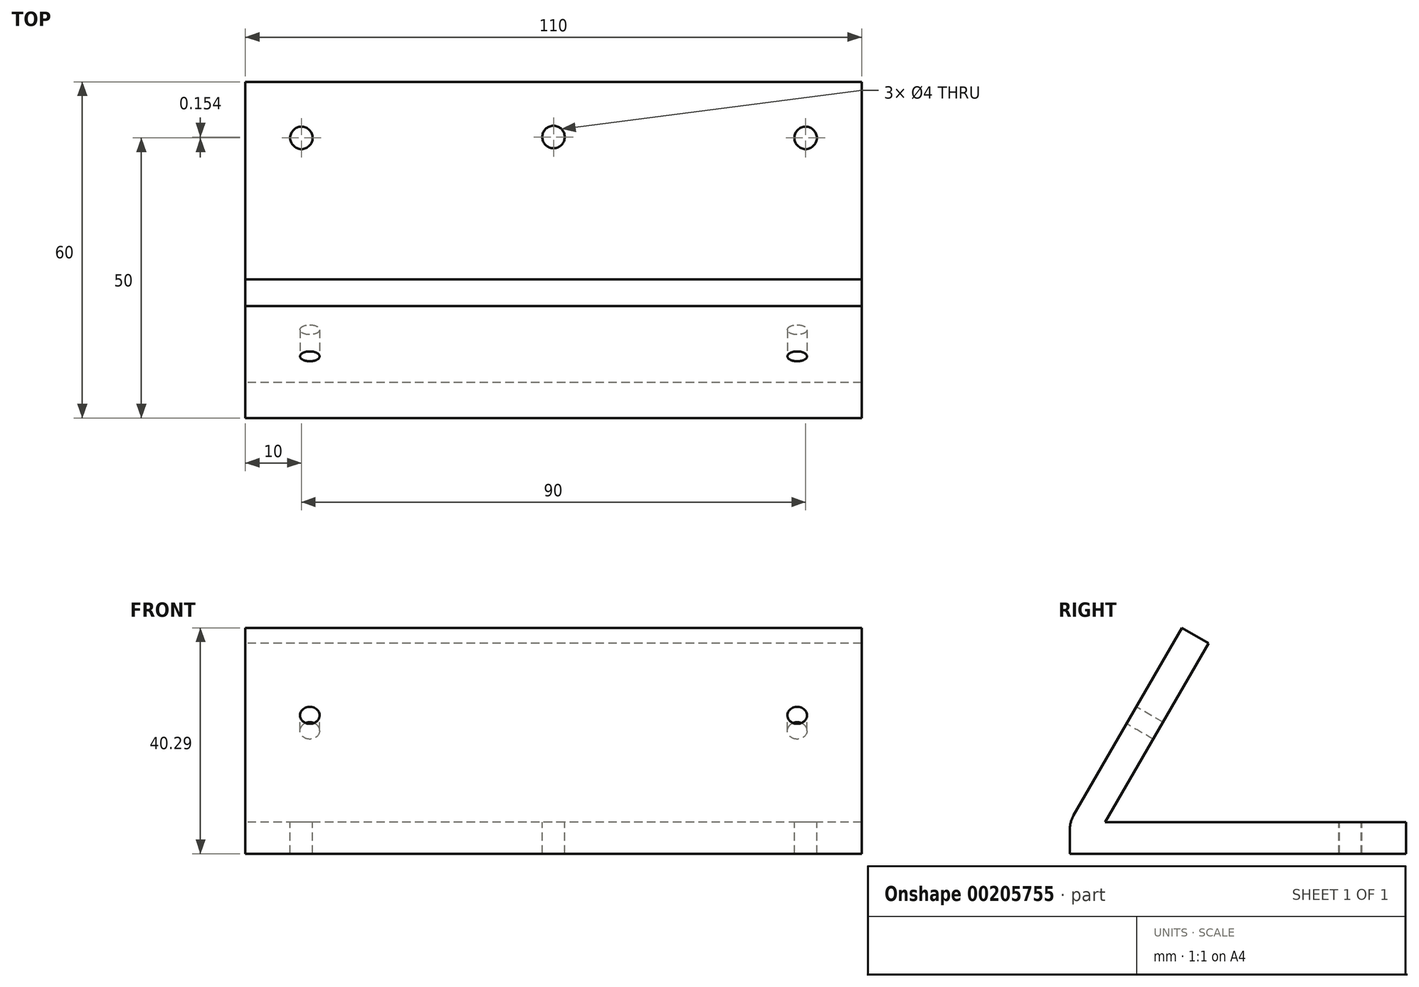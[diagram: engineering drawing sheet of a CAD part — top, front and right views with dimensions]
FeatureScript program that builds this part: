
annotation { "Feature Type Name" : "Feature", "Feature Type Description" : "" }
export const myFeature = defineFeature(function(context is Context, id is Id, definition is map)
    precondition{}
    {
        {
            var Q0;
            Q0=qCreatedBy(makeId("Right.planeOp"),FACE);
            var sketch = newSketch(context, id + "F0", { "sketchPlane" : qUnion([Q0])});
            skLineSegment(sketch, "E0.bottom", {"start": v(6.33, 5.65) * mm, "end": v(60, 5.65) * mm});
            skLineSegment(sketch, "E0.top", {"start": v(0, 0) * mm, "end": v(60, 0) * mm});
            skLineSegment(sketch, "E0.left", {"start": v(0, 5.65) * mm, "end": v(0, 0) * mm});
            skLineSegment(sketch, "E0.right", {"start": v(60, 5.65) * mm, "end": v(60, 0) * mm});
            skLineSegment(sketch, "E1", {"start": v(0, 5.65) * mm, "end": v(20, 40.29) * mm});
            skLineSegment(sketch, "E2", {"start": v(20, 40.29) * mm, "end": v(24.75, 37.55) * mm});
            skLineSegment(sketch, "E3", {"start": v(24.75, 37.55) * mm, "end": v(6.33, 5.65) * mm});
            skSolve(sketch);
        }
        {
            var Q0;
            Q0=makeQuery(id+"F0.imprint","IMPRINT",FACE,{"disambiguationData":[TD([[makeQuery(id+"F0.imprint","IMPRINT",EDGE,{"derivedFrom":sQuery(id+"F0.wireOp",EDGE,"E0.bottom")}),-1.0]])]});
            extrude(context, id + "F1", {"entities" : qUnion([Q0]), "depth" : 110 * mm});
        }
        {
            var Q0;
            Q0=makeQuery(id+"F1.opExtrude","SWEPT_FACE",FACE,{"disambiguationData":[OSD([sQuery(id+"F0.wireOp",EDGE,"E1")])]});
            var sketch = newSketch(context, id + "F2", { "sketchPlane" : qUnion([Q0])});
            skLineSegment(sketch, "E4", {"start": v(0, 26.9) * mm, "end": v(110, 26.9) * mm, "construction": true});
            skCircle(sketch, "E5", {"center": v(11.5, 26.9) * mm, "radius": 1.75 * mm});
            skCircle(sketch, "E6", {"center": v(98.5, 26.9) * mm, "radius": 1.75 * mm});
            skSolve(sketch);
        }
        {
            var Q0;
            Q0=makeQuery(id+"F2.imprint","IMPRINT",FACE,{"disambiguationData":[TD([[makeQuery(id+"F2.imprint","IMPRINT",EDGE,{"derivedFrom":sQuery(id+"F2.wireOp",EDGE,"E5")}),1.0]])]});
            var Q1;
            Q1=makeQuery(id+"F2.imprint","IMPRINT",FACE,{"disambiguationData":[TD([[makeQuery(id+"F2.imprint","IMPRINT",EDGE,{"derivedFrom":sQuery(id+"F2.wireOp",EDGE,"E6")}),1.0]])]});
            extrude(context, id + "F3", {"entities" : qUnion([Q0, Q1]), "operationType" : NewBodyOperationType.REMOVE, "oppositeDirection" : true, "depth" : 8 * mm});
        }
        {
            var Q0;
            Q0=makeQuery(id+"F1.opExtrude","SWEPT_FACE",FACE,{"disambiguationData":[OSD([sQuery(id+"F0.wireOp",EDGE,"E0.bottom")])]});
            var sketch = newSketch(context, id + "F4", { "sketchPlane" : qUnion([Q0])});
            skCircle(sketch, "E7", {"center": v(100, 50) * mm, "radius": 2 * mm});
            skCircle(sketch, "E8", {"center": v(55, 50.15) * mm, "radius": 2 * mm});
            skCircle(sketch, "E9", {"center": v(10, 50) * mm, "radius": 2 * mm});
            skLineSegment(sketch, "E10", {"start": v(110, 50) * mm, "end": v(0, 50) * mm, "construction": true});
            skSolve(sketch);
        }
        {
            var Q0;
            Q0=makeQuery(id+"F4.imprint","IMPRINT",FACE,{"disambiguationData":[TD([[makeQuery(id+"F4.imprint","IMPRINT",EDGE,{"derivedFrom":sQuery(id+"F4.wireOp",EDGE,"E7")}),1.0]])]});
            var Q1;
            Q1=makeQuery(id+"F4.imprint","IMPRINT",FACE,{"disambiguationData":[TD([[makeQuery(id+"F4.imprint","IMPRINT",EDGE,{"derivedFrom":sQuery(id+"F4.wireOp",EDGE,"E8")}),1.0]])]});
            var Q2;
            Q2=makeQuery(id+"F4.imprint","IMPRINT",FACE,{"disambiguationData":[TD([[makeQuery(id+"F4.imprint","IMPRINT",EDGE,{"derivedFrom":sQuery(id+"F4.wireOp",EDGE,"E9")}),1.0]])]});
            extrude(context, id + "F5", {"entities" : qUnion([Q0, Q1, Q2]), "operationType" : NewBodyOperationType.REMOVE, "oppositeDirection" : true, "depth" : 10 * mm});
        }
        {
            var Q0;
            Q0=makeQuery(id+"F1.opExtrude","SWEPT_EDGE",EDGE,{"disambiguationData":[OSD([sQuery(id+"F0.wireOp",EDGE,"E0.left"),sQuery(id+"F0.wireOp",EDGE,"E1")])]});
            fillet(context, id + "F6", {"entities" : qUnion([Q0]), "radius" : 5 * mm, "tangentPropagation" : true, "allowEdgeOverflow" : false});
        }
    });
